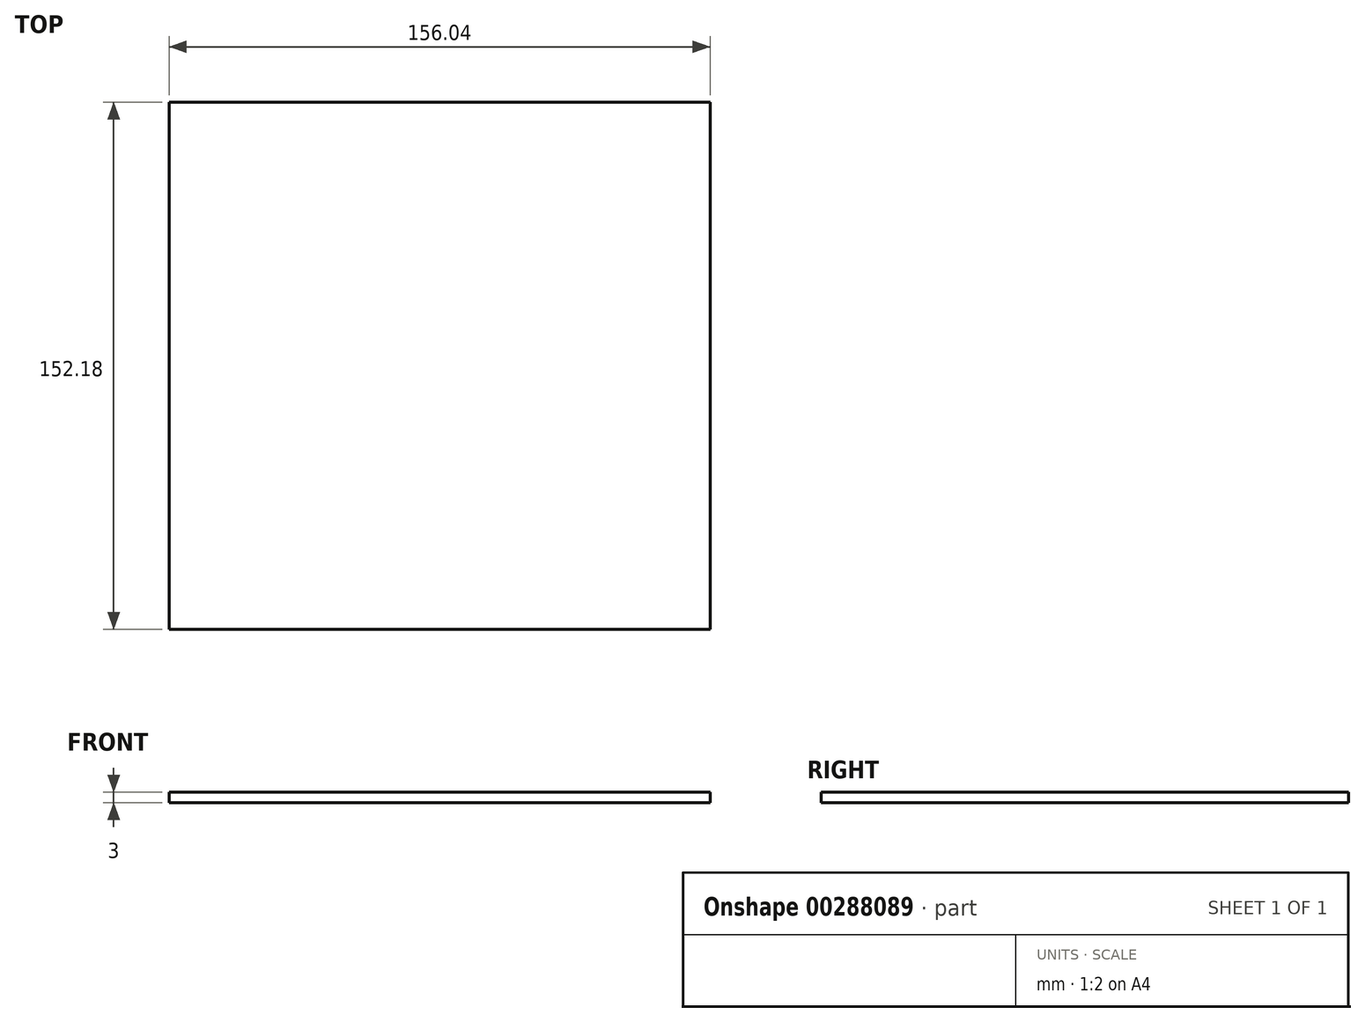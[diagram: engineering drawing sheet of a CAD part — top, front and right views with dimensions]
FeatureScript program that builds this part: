
annotation { "Feature Type Name" : "Feature", "Feature Type Description" : "" }
export const myFeature = defineFeature(function(context is Context, id is Id, definition is map)
    precondition{}
    {
        {
            var Q0;
            Q0=qCreatedBy(makeId("Top.planeOp"),FACE);
            var sketch = newSketch(context, id + "F0", { "sketchPlane" : qUnion([Q0])});
            skLineSegment(sketch, "E0.bottom", {"start": v(78.02, -76.09) * mm, "end": v(-78.02, -76.09) * mm});
            skLineSegment(sketch, "E0.top", {"start": v(78.02, 76.09) * mm, "end": v(-78.02, 76.09) * mm});
            skLineSegment(sketch, "E0.left", {"start": v(78.02, -76.09) * mm, "end": v(78.02, 76.09) * mm});
            skLineSegment(sketch, "E0.right", {"start": v(-78.02, -76.09) * mm, "end": v(-78.02, 76.09) * mm});
            skPoint(sketch, "E0.middle", {"position": v(0, 0) * mm});
            skSolve(sketch);
        }
        {
            var Q0;
            Q0=qSketchRegion(id+"F0",true);
            extrude(context, id + "F1", {"entities" : qUnion([Q0]), "depth" : 3 * mm});
        }
    });
